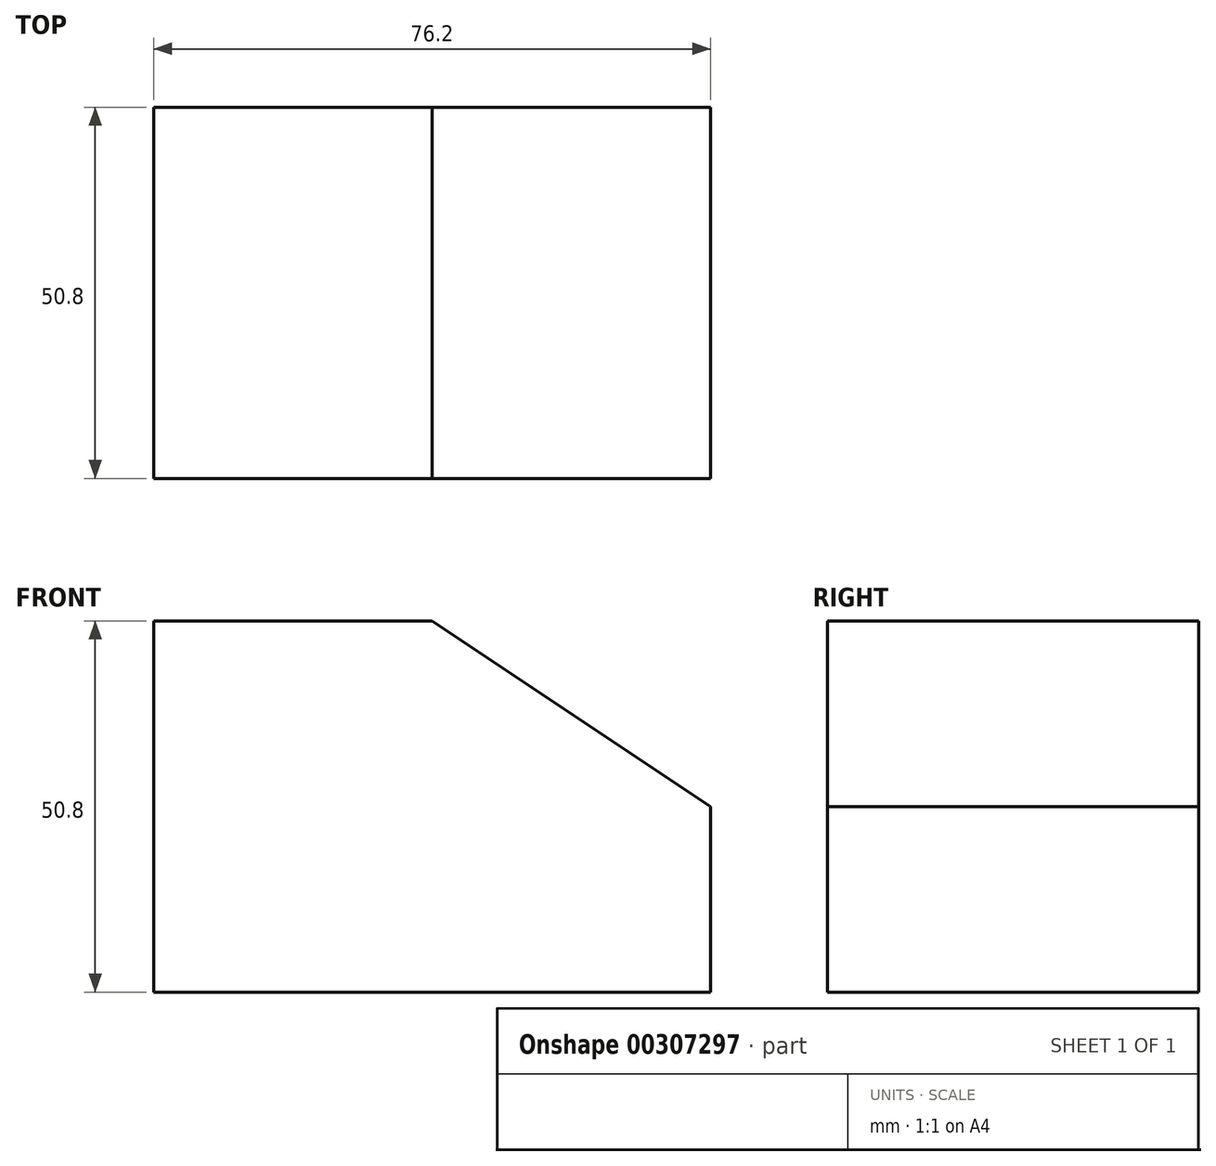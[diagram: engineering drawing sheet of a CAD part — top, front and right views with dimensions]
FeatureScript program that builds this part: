
annotation { "Feature Type Name" : "Feature", "Feature Type Description" : "" }
export const myFeature = defineFeature(function(context is Context, id is Id, definition is map)
    precondition{}
    {
        {
            var Q0;
            Q0=qCreatedBy(makeId("Front.planeOp"),FACE);
            var sketch = newSketch(context, id + "F0", { "sketchPlane" : qUnion([Q0])});
            skLineSegment(sketch, "E0", {"start": v(-39.85, -32.24) * mm, "end": v(36.35, -32.24) * mm});
            skLineSegment(sketch, "E1", {"start": v(36.35, -32.24) * mm, "end": v(36.35, -6.84) * mm});
            skLineSegment(sketch, "E2", {"start": v(-39.85, -32.24) * mm, "end": v(-39.85, 18.56) * mm});
            skLineSegment(sketch, "E3", {"start": v(-39.85, 18.56) * mm, "end": v(-1.75, 18.56) * mm});
            skLineSegment(sketch, "E4", {"start": v(-1.75, 18.56) * mm, "end": v(36.35, -6.84) * mm});
            skSolve(sketch);
        }
        {
            var Q0;
            Q0=makeQuery(id+"F0.imprint","IMPRINT",FACE,{"disambiguationData":[TD([[makeQuery(id+"F0.imprint","IMPRINT",EDGE,{"derivedFrom":sQuery(id+"F0.wireOp",EDGE,"E0")}),1.0]])]});
            extrude(context, id + "F1", {"entities" : qUnion([Q0]), "depth" : 50.8 * mm});
        }
    });
